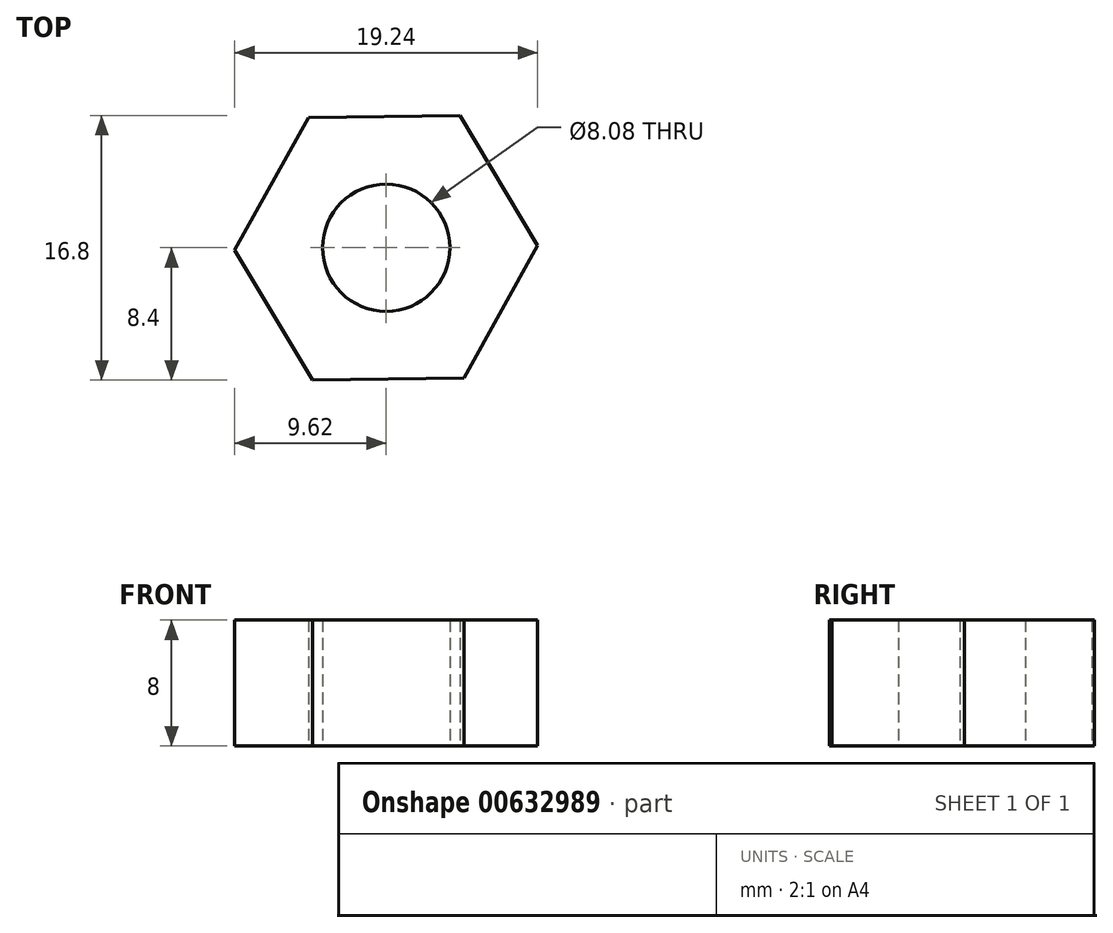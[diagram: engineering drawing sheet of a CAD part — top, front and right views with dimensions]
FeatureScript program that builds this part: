
annotation { "Feature Type Name" : "Feature", "Feature Type Description" : "" }
export const myFeature = defineFeature(function(context is Context, id is Id, definition is map)
    precondition{}
    {
        {
            var Q0;
            Q0=qCreatedBy(makeId("Top.planeOp"),FACE);
            var sketch = newSketch(context, id + "F0", { "sketchPlane" : qUnion([Q0])});
            skCircle(sketch, "E0.cCircle", {"center": v(0, 0) * mm, "radius": 8.33 * mm, "construction": true});
            skLineSegment(sketch, "E0.0", {"start": v(4.69, 8.4) * mm, "end": v(9.62, 0.14) * mm});
            skLineSegment(sketch, "E0.1", {"start": v(9.62, 0.14) * mm, "end": v(4.93, -8.26) * mm});
            skLineSegment(sketch, "E0.2", {"start": v(4.93, -8.26) * mm, "end": v(-4.69, -8.4) * mm});
            skLineSegment(sketch, "E0.3", {"start": v(-4.69, -8.4) * mm, "end": v(-9.62, -0.14) * mm});
            skLineSegment(sketch, "E0.4", {"start": v(-9.62, -0.14) * mm, "end": v(-4.93, 8.26) * mm});
            skLineSegment(sketch, "E0.5", {"start": v(-4.93, 8.26) * mm, "end": v(4.69, 8.4) * mm});
            skPoint(sketch, "E0.0.midPoint", {"position": v(7.15, 4.27) * mm});
            skCircle(sketch, "E1", {"center": v(0, 0) * mm, "radius": 4.04 * mm});
            skSolve(sketch);
        }
        {
            var Q0;
            Q0=qSketchRegion(id+"F0",true);
            extrude(context, id + "F1", {"entities" : qUnion([Q0]), "depth" : 8 * mm});
        }
    });
